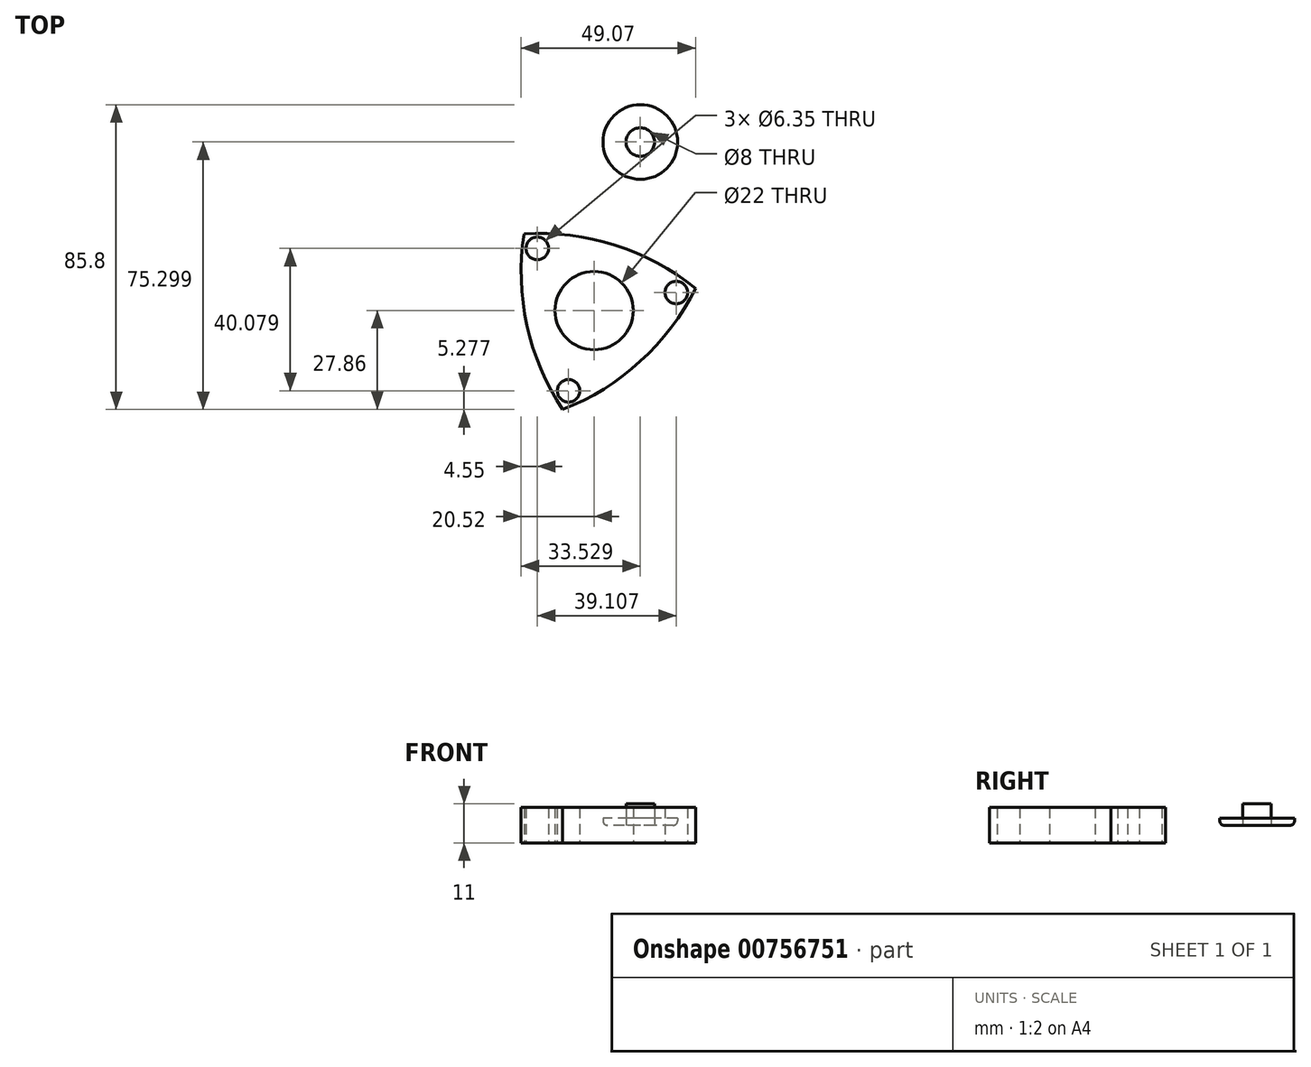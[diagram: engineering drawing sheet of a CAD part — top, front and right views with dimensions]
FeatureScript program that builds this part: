
annotation { "Feature Type Name" : "Feature", "Feature Type Description" : "" }
export const myFeature = defineFeature(function(context is Context, id is Id, definition is map)
    precondition{}
    {
        {
            var Q0;
            Q0=qCreatedBy(makeId("Top.planeOp"),FACE);
            var sketch = newSketch(context, id + "F0", { "sketchPlane" : qUnion([Q0])});
            skCircle(sketch, "E0", {"center": v(0, 0) * mm, "radius": 11 * mm});
            skCircle(sketch, "E1.cCircle", {"center": v(0, 0) * mm, "radius": 14.61 * mm, "construction": true});
            skPoint(sketch, "E1.0.midPoint", {"position": v(4.42, 13.93) * mm});
            skArc(sketch, "E2", {"start": v(28.55, 6.27) * mm, "mid": v(5.85, 18.42) * mm, "end": v(-19.7, 21.59) * mm});
            skArc(sketch, "E3", {"start": v(-8.84, -27.86) * mm, "mid": v(13.03, -14.28) * mm, "end": v(28.55, 6.27) * mm});
            skArc(sketch, "E4", {"start": v(-19.7, 21.59) * mm, "mid": v(-18.88, -4.15) * mm, "end": v(-8.84, -27.86) * mm});
            skCircle(sketch, "E5", {"center": v(-7.17, -22.58) * mm, "radius": 3.18 * mm});
            skCircle(sketch, "E6", {"center": v(23.14, 5.08) * mm, "radius": 3.18 * mm});
            skCircle(sketch, "E7", {"center": v(-15.97, 17.5) * mm, "radius": 3.18 * mm});
            skSolve(sketch);
        }
        {
            var Q0;
            Q0=makeQuery(id+"F0.imprint","IMPRINT",FACE,{"disambiguationData":[TD([[makeQuery(id+"F0.imprint","IMPRINT",EDGE,{"derivedFrom":sQuery(id+"F0.wireOp",EDGE,"E0")}),-1.0]])]});
            extrude(context, id + "F1", {"entities" : qUnion([Q0]), "depth" : 5 * mm, "offsetDistance" : 25.4 * mm, "hasSecondDirection" : true, "secondDirectionOppositeDirection" : true, "secondDirectionDepth" : 5 * mm});
        }
        {
            var Q0;
            Q0=qCreatedBy(makeId("Top.planeOp"),FACE);
            var sketch = newSketch(context, id + "F2", { "sketchPlane" : qUnion([Q0])});
            skCircle(sketch, "E8", {"center": v(13, 47.44) * mm, "radius": 10.5 * mm});
            skCircle(sketch, "E9", {"center": v(13, 47.44) * mm, "radius": 4 * mm});
            skSolve(sketch);
        }
        {
            var Q0;
            Q0=makeQuery(id+"F2.imprint","IMPRINT",FACE,{"disambiguationData":[TD([[makeQuery(id+"F2.imprint","IMPRINT",EDGE,{"derivedFrom":sQuery(id+"F2.wireOp",EDGE,"E8")}),1.0]])]});
            extrude(context, id + "F3", {"entities" : qUnion([Q0]), "depth" : 2 * mm, "offsetDistance" : 25.4 * mm});
        }
        {
            var Q0;
            Q0=makeQuery(id+"F3.opExtrude","CAP_FACE",FACE,{"disambiguationData":[OSD([sQuery(id+"F2.wireOp",EDGE,"E8")])],"isStart":false});
            var sketch = newSketch(context, id + "F4", { "sketchPlane" : qUnion([Q0])});
            skSolve(sketch);
        }
        {
            var Q0;
            Q0=makeQuery(id+"F4.imprint","IMPRINT",FACE,{"disambiguationData":[TD([[makeQuery(id+"F4.imprint","IMPRINT",EDGE,{"derivedFrom":makeQuery(id+"F3.opExtrude","CAP_EDGE",EDGE,{"disambiguationData":[OSD([sQuery(id+"F2.wireOp",EDGE,"E9")])],"isStart":false})}),1.0]])]});
            extrude(context, id + "F5", {"entities" : qUnion([Q0]), "depth" : 4 * mm, "offsetDistance" : 25.4 * mm, "hasSecondDirection" : true, "secondDirectionOppositeDirection" : true, "secondDirectionDepth" : 2 * mm});
        }
        {
            var Q0;
            Q0=makeQuery(id+"F3.opExtrude","CAP_EDGE",EDGE,{"disambiguationData":[OSD([sQuery(id+"F2.wireOp",EDGE,"E8")])],"isStart":true});
            fillet(context, id + "F6", {"entities" : qUnion([Q0]), "radius" : 1.23 * mm, "tangentPropagation" : true, "allowEdgeOverflow" : false});
        }
    });
